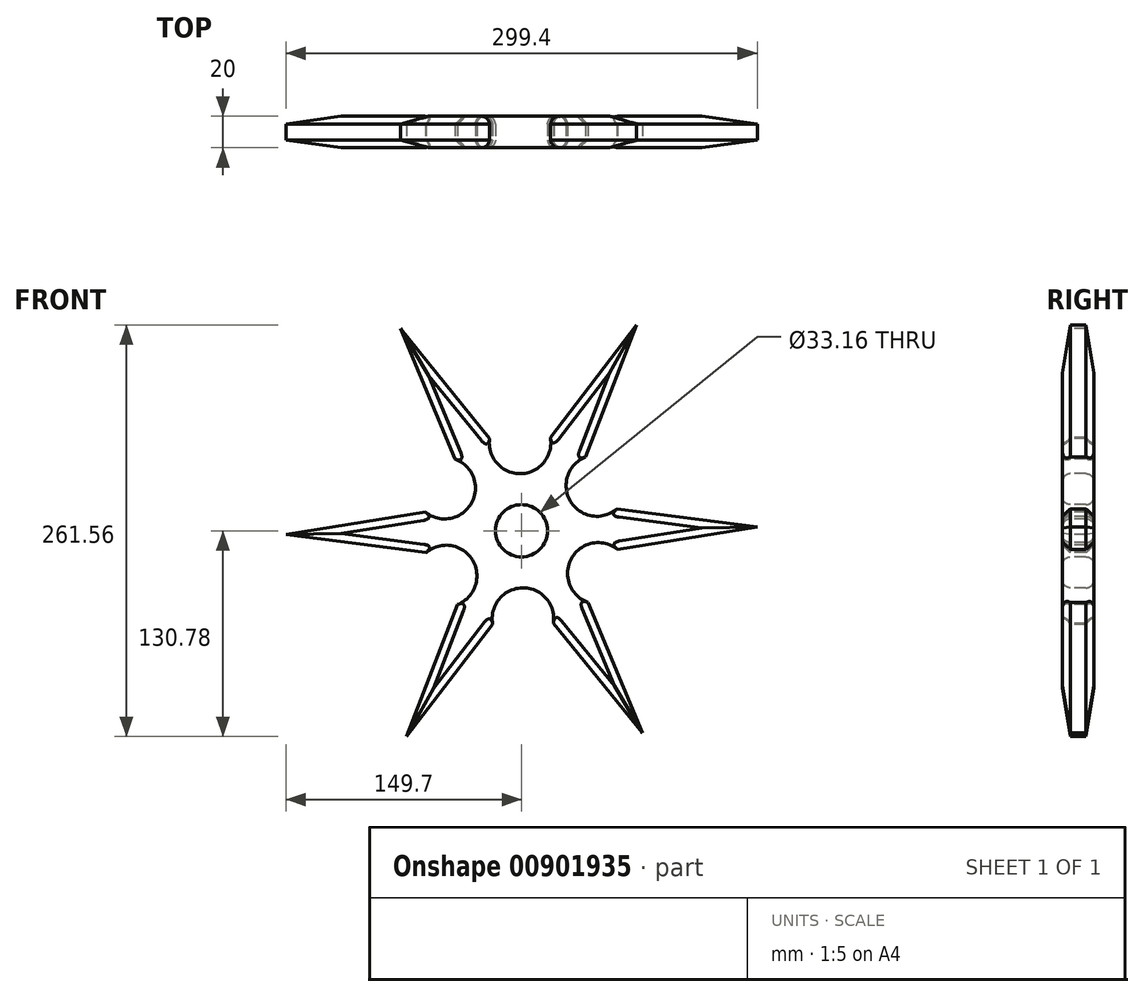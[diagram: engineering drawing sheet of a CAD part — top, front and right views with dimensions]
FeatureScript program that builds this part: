
annotation { "Feature Type Name" : "Feature", "Feature Type Description" : "" }
export const myFeature = defineFeature(function(context is Context, id is Id, definition is map)
    precondition{}
    {
        {
            var Q0;
            Q0=qCreatedBy(makeId("Front.planeOp"),FACE);
            var sketch = newSketch(context, id + "F0", { "sketchPlane" : qUnion([Q0])});
            skArc(sketch, "E0", {"start": v(-61, 11.82) * mm, "mid": v(-62.12, -1.05) * mm, "end": v(-60.57, -13.87) * mm});
            skCircle(sketch, "E1", {"center": v(0, 0) * mm, "radius": 16.58 * mm});
            skCircle(sketch, "E2.cCircle", {"center": v(0, 0) * mm, "radius": 48.33 * mm, "construction": true});
            skLineSegment(sketch, "E2.0", {"start": v(32.04, -37.14) * mm, "end": v(17.7, -45.75) * mm});
            skLineSegment(sketch, "E2.1", {"start": v(-16.15, -46.31) * mm, "end": v(-30.77, -38.2) * mm});
            skLineSegment(sketch, "E2.2", {"start": v(-48.18, -9.17) * mm, "end": v(-48.47, 7.55) * mm});
            skLineSegment(sketch, "E2.3", {"start": v(-32.04, 37.14) * mm, "end": v(-17.7, 45.75) * mm});
            skLineSegment(sketch, "E2.4", {"start": v(16.15, 46.31) * mm, "end": v(30.77, 38.2) * mm});
            skLineSegment(sketch, "E2.5", {"start": v(48.18, 9.17) * mm, "end": v(48.47, -7.55) * mm});
            skPoint(sketch, "E2.0.midPoint", {"position": v(24.87, -41.44) * mm});
            skArc(sketch, "E3", {"start": v(-20.26, 58.74) * mm, "mid": v(-0.6, 36.26) * mm, "end": v(18.27, 59.39) * mm});
            skArc(sketch, "E4.1.0", {"start": v(-61, 11.82) * mm, "mid": v(-31.7, 17.6) * mm, "end": v(-42.3, 45.52) * mm});
            skArc(sketch, "E4.2.0", {"start": v(-40.74, -46.91) * mm, "mid": v(-31.1, -18.66) * mm, "end": v(-60.57, -13.87) * mm});
            skArc(sketch, "E4.3.0", {"start": v(20.26, -58.74) * mm, "mid": v(0.6, -36.26) * mm, "end": v(-18.27, -59.39) * mm});
            skArc(sketch, "E4.4.0", {"start": v(61, -11.82) * mm, "mid": v(31.7, -17.6) * mm, "end": v(42.3, -45.52) * mm});
            skArc(sketch, "E4.5.0", {"start": v(40.74, 46.91) * mm, "mid": v(31.1, 18.66) * mm, "end": v(60.57, 13.87) * mm});
            skArc(sketch, "E5.trimOffspring", {"start": v(-20.26, 58.74) * mm, "mid": v(-31.97, 53.28) * mm, "end": v(-42.3, 45.52) * mm});
            skArc(sketch, "E6.trimOffspring", {"start": v(40.74, 46.91) * mm, "mid": v(30.16, 54.32) * mm, "end": v(18.27, 59.39) * mm});
            skArc(sketch, "E7.trimOffspring", {"start": v(61, -11.82) * mm, "mid": v(62.12, 1.05) * mm, "end": v(60.57, 13.87) * mm});
            skArc(sketch, "E8.trimOffspring", {"start": v(20.26, -58.74) * mm, "mid": v(31.97, -53.28) * mm, "end": v(42.3, -45.52) * mm});
            skArc(sketch, "E9.trimOffspring", {"start": v(-40.74, -46.91) * mm, "mid": v(-30.16, -54.32) * mm, "end": v(-18.27, -59.39) * mm});
            skLineSegment(sketch, "E10", {"start": v(-61, 11.82) * mm, "end": v(-149.7, -2.26) * mm});
            skLineSegment(sketch, "E11", {"start": v(-149.7, -2.26) * mm, "end": v(-60.57, -13.87) * mm});
            skLineSegment(sketch, "E12.1.0", {"start": v(-40.74, -46.91) * mm, "end": v(-72.9, -130.78) * mm});
            skLineSegment(sketch, "E12.1.1", {"start": v(-72.9, -130.78) * mm, "end": v(-18.27, -59.39) * mm});
            skLineSegment(sketch, "E12.2.0", {"start": v(20.26, -58.74) * mm, "end": v(76.8, -128.51) * mm});
            skLineSegment(sketch, "E12.2.1", {"start": v(76.8, -128.51) * mm, "end": v(42.3, -45.52) * mm});
            skLineSegment(sketch, "E12.3.0", {"start": v(61, -11.82) * mm, "end": v(149.7, 2.26) * mm});
            skLineSegment(sketch, "E12.3.1", {"start": v(149.7, 2.26) * mm, "end": v(60.57, 13.87) * mm});
            skLineSegment(sketch, "E12.4.0", {"start": v(40.74, 46.91) * mm, "end": v(72.9, 130.78) * mm});
            skLineSegment(sketch, "E12.4.1", {"start": v(72.9, 130.78) * mm, "end": v(18.27, 59.39) * mm});
            skLineSegment(sketch, "E12.5.0", {"start": v(-20.26, 58.74) * mm, "end": v(-76.8, 128.51) * mm});
            skLineSegment(sketch, "E12.5.1", {"start": v(-76.8, 128.51) * mm, "end": v(-42.3, 45.52) * mm});
            skSolve(sketch);
        }
        {
            var Q0;
            Q0=makeQuery(id+"F0.imprint","IMPRINT",FACE,{"disambiguationData":[TD([[makeQuery(id+"F0.imprint","IMPRINT",EDGE,{"derivedFrom":sQuery(id+"F0.wireOp",EDGE,"E6.trimOffspring")}),-1.0]])]});
            var Q1;
            Q1=makeQuery(id+"F0.imprint","IMPRINT",FACE,{"disambiguationData":[TD([[makeQuery(id+"F0.imprint","IMPRINT",EDGE,{"derivedFrom":sQuery(id+"F0.wireOp",EDGE,"E1")}),-1.0]])]});
            var Q2;
            {var subQ0=sQuery(id+"F0.wireOp",EDGE,"E2.5");Q2=makeQuery(id+"F0.imprint","IMPRINT",FACE,{"disambiguationData":[TD([[makeQuery(id+"F0.imprint","IMPRINT",EDGE,{"derivedFrom":subQ0}),1.0]])]});}
            var Q3;
            {var subQ0=sQuery(id+"F0.wireOp",EDGE,"E2.4");Q3=makeQuery(id+"F0.imprint","IMPRINT",FACE,{"disambiguationData":[TD([[makeQuery(id+"F0.imprint","IMPRINT",EDGE,{"derivedFrom":subQ0}),1.0]])]});}
            var Q4;
            Q4=makeQuery(id+"F0.imprint","IMPRINT",FACE,{"disambiguationData":[TD([[makeQuery(id+"F0.imprint","IMPRINT",EDGE,{"derivedFrom":sQuery(id+"F0.wireOp",EDGE,"E7.trimOffspring")}),-1.0]])]});
            var Q5;
            Q5=makeQuery(id+"F0.imprint","IMPRINT",FACE,{"disambiguationData":[TD([[makeQuery(id+"F0.imprint","IMPRINT",EDGE,{"derivedFrom":sQuery(id+"F0.wireOp",EDGE,"E8.trimOffspring")}),-1.0]])]});
            var Q6;
            {var subQ0=sQuery(id+"F0.wireOp",EDGE,"E2.0");Q6=makeQuery(id+"F0.imprint","IMPRINT",FACE,{"disambiguationData":[TD([[makeQuery(id+"F0.imprint","IMPRINT",EDGE,{"derivedFrom":subQ0}),1.0]])]});}
            var Q7;
            {var subQ0=sQuery(id+"F0.wireOp",EDGE,"E2.1");Q7=makeQuery(id+"F0.imprint","IMPRINT",FACE,{"disambiguationData":[TD([[makeQuery(id+"F0.imprint","IMPRINT",EDGE,{"derivedFrom":subQ0}),1.0]])]});}
            var Q8;
            Q8=makeQuery(id+"F0.imprint","IMPRINT",FACE,{"disambiguationData":[TD([[makeQuery(id+"F0.imprint","IMPRINT",EDGE,{"derivedFrom":sQuery(id+"F0.wireOp",EDGE,"E9.trimOffspring")}),-1.0]])]});
            var Q9;
            Q9=makeQuery(id+"F0.imprint","IMPRINT",FACE,{"disambiguationData":[TD([[makeQuery(id+"F0.imprint","IMPRINT",EDGE,{"derivedFrom":sQuery(id+"F0.wireOp",EDGE,"E0")}),-1.0]])]});
            var Q10;
            {var subQ0=sQuery(id+"F0.wireOp",EDGE,"E0");Q10=makeQuery(id+"F0.imprint","IMPRINT",FACE,{"disambiguationData":[TD([[makeQuery(id+"F0.imprint","IMPRINT",EDGE,{"derivedFrom":subQ0}),1.0]])]});}
            var Q11;
            {var subQ0=sQuery(id+"F0.wireOp",EDGE,"E2.3");Q11=makeQuery(id+"F0.imprint","IMPRINT",FACE,{"disambiguationData":[TD([[makeQuery(id+"F0.imprint","IMPRINT",EDGE,{"derivedFrom":subQ0}),1.0]])]});}
            var Q12;
            Q12=makeQuery(id+"F0.imprint","IMPRINT",FACE,{"disambiguationData":[TD([[makeQuery(id+"F0.imprint","IMPRINT",EDGE,{"derivedFrom":sQuery(id+"F0.wireOp",EDGE,"E5.trimOffspring")}),-1.0]])]});
            extrude(context, id + "F1", {"entities" : qUnion([Q0, Q1, Q2, Q3, Q4, Q5, Q6, Q7, Q8, Q9, Q10, Q11, Q12]), "oppositeDirection" : true, "depth" : 20 * mm, "offsetDistance" : 25 * mm});
        }
        {
            var Q0;
            Q0=makeQuery(id+"F1.opExtrude","CAP_EDGE",EDGE,{"disambiguationData":[OSD([sQuery(id+"F0.wireOp",EDGE,"E12.4.0")])],"isStart":true});
            var Q1;
            Q1=makeQuery(id+"F1.opExtrude","CAP_EDGE",EDGE,{"disambiguationData":[OSD([sQuery(id+"F0.wireOp",EDGE,"E12.4.1")])],"isStart":true});
            var Q2;
            Q2=makeQuery(id+"F1.opExtrude","CAP_EDGE",EDGE,{"disambiguationData":[OSD([sQuery(id+"F0.wireOp",EDGE,"E12.4.0")])],"isStart":false});
            var Q3;
            Q3=makeQuery(id+"F1.opExtrude","CAP_EDGE",EDGE,{"disambiguationData":[OSD([sQuery(id+"F0.wireOp",EDGE,"E12.4.1")])],"isStart":false});
            var Q4;
            Q4=makeQuery(id+"F1.opExtrude","CAP_EDGE",EDGE,{"disambiguationData":[OSD([sQuery(id+"F0.wireOp",EDGE,"E12.5.0")])],"isStart":true});
            var Q5;
            Q5=makeQuery(id+"F1.opExtrude","CAP_EDGE",EDGE,{"disambiguationData":[OSD([sQuery(id+"F0.wireOp",EDGE,"E12.5.0")])],"isStart":false});
            var Q6;
            Q6=makeQuery(id+"F1.opExtrude","CAP_EDGE",EDGE,{"disambiguationData":[OSD([sQuery(id+"F0.wireOp",EDGE,"E12.5.1")])],"isStart":true});
            var Q7;
            Q7=makeQuery(id+"F1.opExtrude","CAP_EDGE",EDGE,{"disambiguationData":[OSD([sQuery(id+"F0.wireOp",EDGE,"E12.5.1")])],"isStart":false});
            var Q8;
            Q8=makeQuery(id+"F1.opExtrude","CAP_EDGE",EDGE,{"disambiguationData":[OSD([sQuery(id+"F0.wireOp",EDGE,"E10")])],"isStart":true});
            var Q9;
            Q9=makeQuery(id+"F1.opExtrude","CAP_EDGE",EDGE,{"disambiguationData":[OSD([sQuery(id+"F0.wireOp",EDGE,"E11")])],"isStart":true});
            var Q10;
            Q10=makeQuery(id+"F1.opExtrude","CAP_EDGE",EDGE,{"disambiguationData":[OSD([sQuery(id+"F0.wireOp",EDGE,"E11")])],"isStart":false});
            var Q11;
            Q11=makeQuery(id+"F1.opExtrude","CAP_EDGE",EDGE,{"disambiguationData":[OSD([sQuery(id+"F0.wireOp",EDGE,"E10")])],"isStart":false});
            var Q12;
            Q12=makeQuery(id+"F1.opExtrude","CAP_EDGE",EDGE,{"disambiguationData":[OSD([sQuery(id+"F0.wireOp",EDGE,"E12.3.0")])],"isStart":false});
            var Q13;
            Q13=makeQuery(id+"F1.opExtrude","CAP_EDGE",EDGE,{"disambiguationData":[OSD([sQuery(id+"F0.wireOp",EDGE,"E12.3.1")])],"isStart":false});
            var Q14;
            Q14=makeQuery(id+"F1.opExtrude","CAP_EDGE",EDGE,{"disambiguationData":[OSD([sQuery(id+"F0.wireOp",EDGE,"E12.3.1")])],"isStart":true});
            var Q15;
            Q15=makeQuery(id+"F1.opExtrude","CAP_EDGE",EDGE,{"disambiguationData":[OSD([sQuery(id+"F0.wireOp",EDGE,"E12.3.0")])],"isStart":true});
            var Q16;
            Q16=makeQuery(id+"F1.opExtrude","CAP_EDGE",EDGE,{"disambiguationData":[OSD([sQuery(id+"F0.wireOp",EDGE,"E12.2.1")])],"isStart":true});
            var Q17;
            Q17=makeQuery(id+"F1.opExtrude","CAP_EDGE",EDGE,{"disambiguationData":[OSD([sQuery(id+"F0.wireOp",EDGE,"E12.2.0")])],"isStart":true});
            var Q18;
            Q18=makeQuery(id+"F1.opExtrude","CAP_EDGE",EDGE,{"disambiguationData":[OSD([sQuery(id+"F0.wireOp",EDGE,"E12.1.0")])],"isStart":true});
            var Q19;
            Q19=makeQuery(id+"F1.opExtrude","CAP_EDGE",EDGE,{"disambiguationData":[OSD([sQuery(id+"F0.wireOp",EDGE,"E12.1.1")])],"isStart":true});
            var Q20;
            Q20=makeQuery(id+"F1.opExtrude","CAP_EDGE",EDGE,{"disambiguationData":[OSD([sQuery(id+"F0.wireOp",EDGE,"E12.1.1")])],"isStart":false});
            var Q21;
            Q21=makeQuery(id+"F1.opExtrude","CAP_EDGE",EDGE,{"disambiguationData":[OSD([sQuery(id+"F0.wireOp",EDGE,"E12.1.0")])],"isStart":false});
            var Q22;
            Q22=makeQuery(id+"F1.opExtrude","CAP_EDGE",EDGE,{"disambiguationData":[OSD([sQuery(id+"F0.wireOp",EDGE,"E12.2.0")])],"isStart":false});
            var Q23;
            Q23=makeQuery(id+"F1.opExtrude","CAP_EDGE",EDGE,{"disambiguationData":[OSD([sQuery(id+"F0.wireOp",EDGE,"E12.2.1")])],"isStart":false});
            chamfer(context, id + "F2", {"entities" : qUnion([Q0, Q1, Q2, Q3, Q4, Q5, Q6, Q7, Q8, Q9, Q10, Q11, Q12, Q13, Q14, Q15, Q16, Q17, Q18, Q19, Q20, Q21, Q22, Q23]), "width" : 5 * mm, "tangentPropagation" : true});
        }
        {
            var Q0;
            Q0=makeQuery(id+"F1.opExtrude","CAP_EDGE",EDGE,{"disambiguationData":[OSD([sQuery(id+"F0.wireOp",EDGE,"E4.1.0")])],"isStart":true});
            var Q1;
            Q1=makeQuery(id+"F1.opExtrude","CAP_EDGE",EDGE,{"disambiguationData":[OSD([sQuery(id+"F0.wireOp",EDGE,"E4.1.0")])],"isStart":false});
            var Q2;
            Q2=makeQuery(id+"F1.opExtrude","CAP_EDGE",EDGE,{"disambiguationData":[OSD([sQuery(id+"F0.wireOp",EDGE,"E3")])],"isStart":true});
            var Q3;
            Q3=makeQuery(id+"F1.opExtrude","CAP_EDGE",EDGE,{"disambiguationData":[OSD([sQuery(id+"F0.wireOp",EDGE,"E4.2.0")])],"isStart":true});
            var Q4;
            Q4=makeQuery(id+"F1.opExtrude","CAP_EDGE",EDGE,{"disambiguationData":[OSD([sQuery(id+"F0.wireOp",EDGE,"E4.3.0")])],"isStart":true});
            var Q5;
            Q5=makeQuery(id+"F1.opExtrude","CAP_EDGE",EDGE,{"disambiguationData":[OSD([sQuery(id+"F0.wireOp",EDGE,"E4.4.0")])],"isStart":true});
            var Q6;
            Q6=makeQuery(id+"F1.opExtrude","CAP_EDGE",EDGE,{"disambiguationData":[OSD([sQuery(id+"F0.wireOp",EDGE,"E4.5.0")])],"isStart":true});
            var Q7;
            Q7=makeQuery(id+"F1.opExtrude","CAP_EDGE",EDGE,{"disambiguationData":[OSD([sQuery(id+"F0.wireOp",EDGE,"E1")])],"isStart":true});
            var Q8;
            Q8=makeQuery(id+"F1.opExtrude","CAP_EDGE",EDGE,{"disambiguationData":[OSD([sQuery(id+"F0.wireOp",EDGE,"E4.3.0")])],"isStart":false});
            var Q9;
            Q9=makeQuery(id+"F1.opExtrude","CAP_EDGE",EDGE,{"disambiguationData":[OSD([sQuery(id+"F0.wireOp",EDGE,"E4.2.0")])],"isStart":false});
            var Q10;
            Q10=makeQuery(id+"F1.opExtrude","CAP_EDGE",EDGE,{"disambiguationData":[OSD([sQuery(id+"F0.wireOp",EDGE,"E4.4.0")])],"isStart":false});
            var Q11;
            Q11=makeQuery(id+"F1.opExtrude","CAP_EDGE",EDGE,{"disambiguationData":[OSD([sQuery(id+"F0.wireOp",EDGE,"E4.5.0")])],"isStart":false});
            var Q12;
            Q12=makeQuery(id+"F1.opExtrude","CAP_EDGE",EDGE,{"disambiguationData":[OSD([sQuery(id+"F0.wireOp",EDGE,"E3")])],"isStart":false});
            var Q13;
            Q13=makeQuery(id+"F1.opExtrude","CAP_EDGE",EDGE,{"disambiguationData":[OSD([sQuery(id+"F0.wireOp",EDGE,"E1")])],"isStart":false});
            fillet(context, id + "F3", {"entities" : qUnion([Q0, Q1, Q2, Q3, Q4, Q5, Q6, Q7, Q8, Q9, Q10, Q11, Q12, Q13]), "radius" : 5 * mm, "tangentPropagation" : true, "allowEdgeOverflow" : false});
        }
    });
